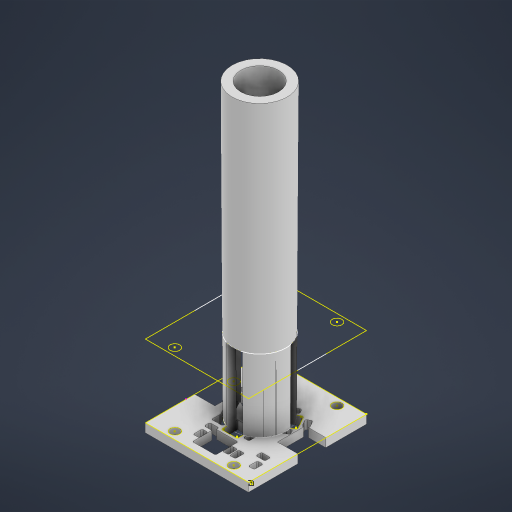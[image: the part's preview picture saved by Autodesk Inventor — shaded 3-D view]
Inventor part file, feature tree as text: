
AUTODESK INVENTOR PART (.ipt)
format: ipt  version: 2024.1 (Build 281209000, 209)  size: 1,723,392 bytes
history: native  units: mm
features: projected_geometry x22, sketch x17, extrude x11, plane x2, loft x2
ambient origin geometry x8: Origin, YZ Plane, XZ Plane, XY Plane, X Axis, Y Axis, Z Axis, Center Point
bodies: Solid1 (feature_tree)
feature tree (54):
  extrude  "Extrusion1"  Depth=3.0mm
  extrude  "Extrusion2"  TaperAngle=0.0deg  [1 undecoded]
  extrude  "Extrusion3"  Depth=10.0mm TaperAngle=0.0deg
  extrude  "Extrusion4"  Depth=0.5mm
  extrude  "Extrusion5"  Depth=0.5mm
  sketch  "Sketch6"  dims[d14=0.5mm d15=0.5mm]
  plane  "Work Plane1"
  loft  "Loft1"
  loft  "Loft2"
  extrude  "Extrusion6"  Depth=0.5mm
  extrude  "Extrusion8"  Depth=0.5mm
  extrude  "Extrusion9"  Depth=0.5mm
  extrude  "Extrusion10"  Depth=0.5mm
  extrude  "Extrusion11"  Depth=0.5mm
  extrude  "Extrusion12"  Depth=0.5mm
  plane  "Work Plane2"
  sketch  "Sketch19"  dims[d32=0.5mm]
  sketch  "Sketch20"  dims[d33=0.5mm d34=0.5mm d35=0.5mm d36=0.5mm d37=0.5mm d38=10.0mm d39=0.0mm d40=12.0mm d41=100.0mm d42=13.0mm d43=3.0mm d44=3.0mm d45=0.0mm d46=90.0deg d47=0.0mm d48=90.0deg d49=13.0mm d50=0.0mm d51=90.0deg d52=0.0mm d53=90.0deg d55=7.0mm d56=17.0mm d57=14.0mm d58=0.0mm d59=0.0mm d64=25.0mm d65=0.0mm d66=25.0mm d67=0.0mm d68=25.0mm d69=0.0mm d70=3.0mm d71=1.0mm d72=1.0mm d73=10.0mm d74=0.0mm d75=10.0mm d76=0.0mm]
  sketch  "Sketch1"  dims[d0=3.0mm d1=0.0mm d2=0.2mm]
  sketch  "Sketch2"  dims[d3=1.0mm d4=0.0mm d5=0.0mm]
  sketch  "Sketch3"  dims[d6=10.0mm d7=0.0mm d8=10.0mm d9=0.0mm]
  sketch  "Sketch4"  dims[d10=0.5mm d11=0.5mm]
  sketch  "Sketch5"  dims[d12=0.5mm d13=0.5mm]
  sketch  "Sketch7"  dims[d16=0.5mm d17=0.5mm]
  sketch  "Sketch8"  dims[d18=0.5mm d19=0.5mm]
  sketch  "Sketch9"  dims[d20=0.5mm d21=0.5mm]
  sketch  "Sketch11"  dims[d22=0.5mm d23=0.5mm]
  sketch  "Sketch13"  dims[d24=0.5mm d25=0.5mm]
  projected_geometry  "Projected Loop2"
  projected_geometry  "Projected Loop3"
  projected_geometry  "Projected Loop4"
  projected_geometry  "Projected Loop5"
  projected_geometry  "Projected Loop6"
  projected_geometry  "Projected Loop7"
  projected_geometry  "Projected Loop8"
  projected_geometry  "Projected Loop9"
  projected_geometry  "Projected Loop10"
  projected_geometry  "Projected Loop11"
  projected_geometry  "Projected Loop12"
  projected_geometry  "Projected Loop13"
  projected_geometry  "Projected Loop14"
  projected_geometry  "Projected Loop15"
  projected_geometry  "Projected Loop16"
  projected_geometry  "Projected Loop17"
  sketch  "Sketch14"  dims[d26=0.5mm d27=0.5mm]
  sketch  "Sketch15"  dims[d28=0.5mm d29=0.5mm]
  projected_geometry  "Projected Loop18"
  sketch  "Sketch16"  dims[d30=0.5mm]
  sketch  "Sketch17"  dims[d31=0.5mm]
  projected_geometry  "Projected Loop19"
  projected_geometry  "Project Cut Edges1"
  projected_geometry  "Project Cut Edges2"
  projected_geometry  "Project Cut Edges3"
  projected_geometry  "Project Cut Edges5"
note: 1 required parameter value undecoded (feature->parameter linkage not recoverable at this tier; creation-order binding heuristic only, values carry confidence <= 0.55)
